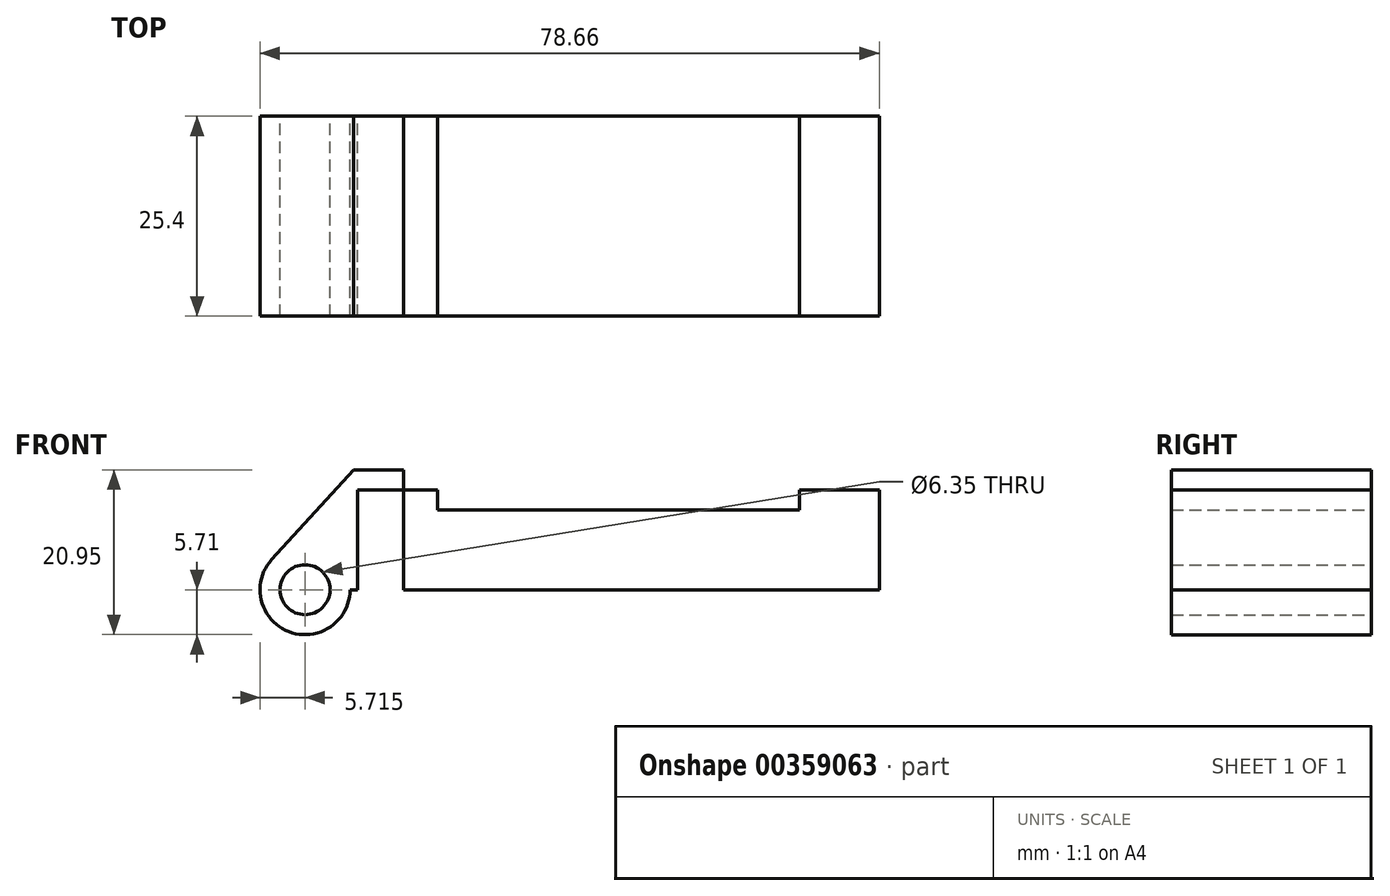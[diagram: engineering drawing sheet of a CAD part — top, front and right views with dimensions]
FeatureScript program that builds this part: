
annotation { "Feature Type Name" : "Feature", "Feature Type Description" : "" }
export const myFeature = defineFeature(function(context is Context, id is Id, definition is map)
    precondition{}
    {
        {
            var Q0;
            Q0=qCreatedBy(makeId("Front.planeOp"),FACE);
            var sketch = newSketch(context, id + "F0", { "sketchPlane" : qUnion([Q0])});
            skLineSegment(sketch, "E0", {"start": v(0, 0) * mm, "end": v(0, 12.7) * mm});
            skLineSegment(sketch, "E1", {"start": v(0, 12.7) * mm, "end": v(10.16, 12.7) * mm});
            skLineSegment(sketch, "E2", {"start": v(10.16, 12.7) * mm, "end": v(10.16, 10.16) * mm});
            skLineSegment(sketch, "E3", {"start": v(10.16, 10.16) * mm, "end": v(56.13, 10.16) * mm});
            skLineSegment(sketch, "E4", {"start": v(56.13, 10.16) * mm, "end": v(56.13, 12.7) * mm});
            skLineSegment(sketch, "E5", {"start": v(56.13, 12.7) * mm, "end": v(66.3, 12.7) * mm});
            skLineSegment(sketch, "E6", {"start": v(66.3, 12.7) * mm, "end": v(66.3, 0) * mm});
            skLineSegment(sketch, "E7", {"start": v(66.3, 0) * mm, "end": v(0, 0) * mm});
            skLineSegment(sketch, "E8", {"start": v(5.84, 15.24) * mm, "end": v(-0.5, 15.24) * mm});
            skLineSegment(sketch, "E9", {"start": v(-0.5, 15.24) * mm, "end": v(-10.88, 3.85) * mm});
            skLineSegment(sketch, "E10", {"start": v(0, 0) * mm, "end": v(-6.65, 0) * mm});
            skCircle(sketch, "E11", {"center": v(-6.65, 0) * mm, "radius": 5.72 * mm});
            skCircle(sketch, "E12", {"center": v(-6.65, 0) * mm, "radius": 3.18 * mm});
            skLineSegment(sketch, "E13", {"start": v(5.84, 15.24) * mm, "end": v(5.84, -9.4) * mm});
            skLineSegment(sketch, "E14", {"start": v(5.84, -9.4) * mm, "end": v(-8.18, -5.5) * mm});
            skSolve(sketch);
        }
        {
            var Q0;
            {var subQ1=sQuery(id+"F0.wireOp",EDGE,"E0");Q0=makeQuery(id+"F0.imprint","IMPRINT",FACE,{"disambiguationData":[TD([[makeQuery(id+"F0.imprint","IMPRINT",EDGE,{"derivedFrom":subQ1}),1.0]])]});}
            var Q1;
            {var subQ5=sQuery(id+"F0.wireOp",EDGE,"E12");Q1=makeQuery(id+"F0.imprint","IMPRINT",FACE,{"disambiguationData":[TD([[makeQuery(id+"F0.imprint","IMPRINT",EDGE,{"derivedFrom":subQ5}),-1.0]])]});}
            extrude(context, id + "F1", {"entities" : qUnion([Q0, Q1]), "depth" : 25.4 * mm});
        }
        {
            var Q0;
            {var subQ0=sQuery(id+"F0.wireOp",EDGE,"E2");Q0=makeQuery(id+"F0.imprint","IMPRINT",FACE,{"disambiguationData":[TD([[makeQuery(id+"F0.imprint","IMPRINT",EDGE,{"derivedFrom":subQ0}),-1.0]])]});}
            extrude(context, id + "F2", {"entities" : qUnion([Q0]), "depth" : 25.4 * mm});
        }
    });
